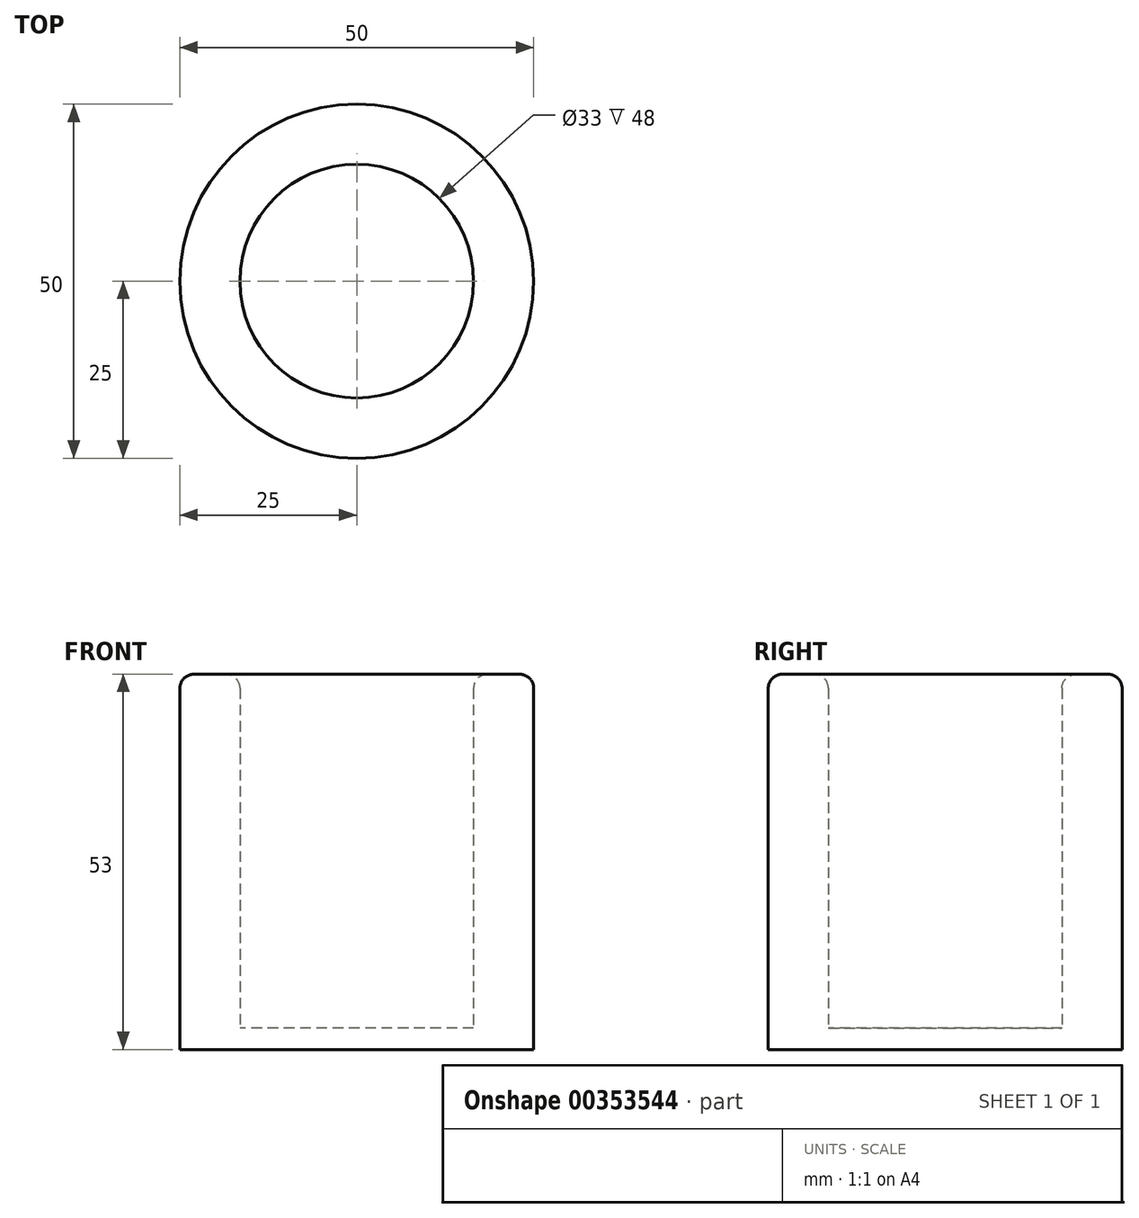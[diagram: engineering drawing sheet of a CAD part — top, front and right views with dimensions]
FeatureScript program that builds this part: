
annotation { "Feature Type Name" : "Feature", "Feature Type Description" : "" }
export const myFeature = defineFeature(function(context is Context, id is Id, definition is map)
    precondition{}
    {
        {
            var Q0;
            Q0=qCreatedBy(makeId("Top.planeOp"),FACE);
            var sketch = newSketch(context, id + "F0", { "sketchPlane" : qUnion([Q0])});
            skCircle(sketch, "E0", {"center": v(0, 0) * mm, "radius": 25 * mm});
            skSolve(sketch);
        }
        {
            var Q0;
            Q0 = qSketchRegion(id + "F0", true);
            extrude(context, id + "F1", {"entities" : qUnion([Q0]), "depth" : 3 * mm});
        }
        {
            var Q0;
            Q0=makeQuery(id+"F1.opExtrude","CAP_FACE",FACE,{"disambiguationData":[OSD([sQuery(id+"F0.wireOp",EDGE,"E0")])],"isStart":false});
            var sketch = newSketch(context, id + "F2", { "sketchPlane" : qUnion([Q0])});
            skCircle(sketch, "E1", {"center": v(0, 0) * mm, "radius": 16.5 * mm});
            skSolve(sketch);
        }
        {
            var Q0;
            Q0=makeQuery(id+"F2.imprint","IMPRINT",FACE,{"disambiguationData":[TD([[makeQuery(id+"F2.imprint","IMPRINT",EDGE,{"derivedFrom":sQuery(id+"F2.wireOp",EDGE,"E1")}),-1.0]])]});
            extrude(context, id + "F3", {"entities" : qUnion([Q0]), "operationType" : NewBodyOperationType.ADD, "depth" : 50 * mm});
        }
        {
            var Q0;
            Q0=makeQuery(id+"F3.opExtrude","CAP_EDGE",EDGE,{"disambiguationData":[OSD([sQuery(id+"F0.wireOp",EDGE,"E0")])],"isStart":false});
            var Q1;
            Q1=makeQuery(id+"F3.opExtrude","CAP_EDGE",EDGE,{"disambiguationData":[OSD([sQuery(id+"F2.wireOp",EDGE,"E1")])],"isStart":false});
            var Q2;
            Q2=makeQuery(id+"F3.opExtrude","CAP_EDGE",EDGE,{"disambiguationData":[OSD([sQuery(id+"F2.wireOp",EDGE,"E1")])],"isStart":true});
            fillet(context, id + "F4", {"entities" : qUnion([Q0, Q1, Q2]), "radius" : 2 * mm, "tangentPropagation" : true, "allowEdgeOverflow" : false});
        }
    });
